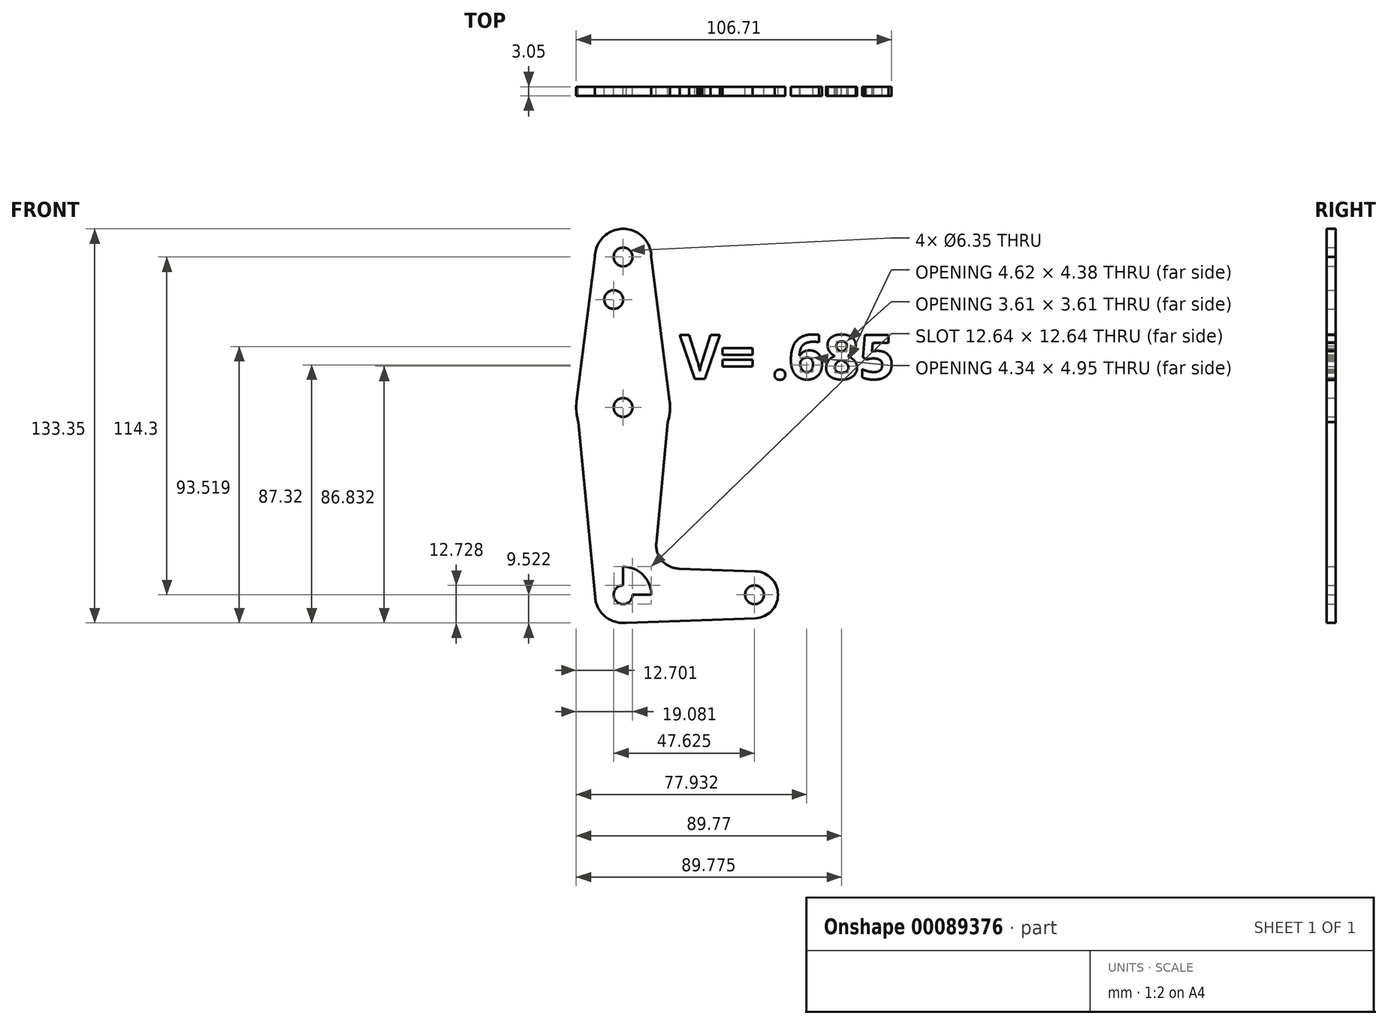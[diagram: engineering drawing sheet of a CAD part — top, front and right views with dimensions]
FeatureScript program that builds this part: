
annotation { "Feature Type Name" : "Feature", "Feature Type Description" : "" }
export const myFeature = defineFeature(function(context is Context, id is Id, definition is map)
    precondition{}
    {
        {
            var Q0;
            Q0=qCreatedBy(makeId("Front.planeOp"),FACE);
            var sketch = newSketch(context, id + "F0", { "sketchPlane" : qUnion([Q0])});
            skCircle(sketch, "E0", {"center": v(-39.47, 60.23) * mm, "radius": 9.53 * mm});
            skCircle(sketch, "E1", {"center": v(-39.47, 9.3) * mm, "radius": 15.88 * mm});
            skLineSegment(sketch, "E2", {"start": v(-39.47, 60.23) * mm, "end": v(-39.47, -54.07) * mm});
            skLineSegment(sketch, "E3", {"start": v(-39.47, -54.07) * mm, "end": v(4.98, -54.07) * mm});
            skCircle(sketch, "E4", {"center": v(-39.47, -54.07) * mm, "radius": 9.53 * mm});
            skCircle(sketch, "E5", {"center": v(4.98, -54.07) * mm, "radius": 7.94 * mm});
            skLineSegment(sketch, "E6", {"start": v(-49, 60.23) * mm, "end": v(-55.22, 11.3) * mm});
            skLineSegment(sketch, "E7", {"start": v(-55.22, 11.3) * mm, "end": v(-48.96, -54.96) * mm});
            skLineSegment(sketch, "E8", {"start": v(-29.95, 60.21) * mm, "end": v(-23.73, 11.3) * mm});
            skLineSegment(sketch, "E9", {"start": v(-23.73, 11.3) * mm, "end": v(-28.25, -36.52) * mm});
            skLineSegment(sketch, "E10", {"start": v(-20.62, -45.21) * mm, "end": v(5.26, -46.14) * mm});
            skCircle(sketch, "E11", {"center": v(-39.47, 60.23) * mm, "radius": 3.18 * mm});
            skCircle(sketch, "E12", {"center": v(-39.47, 9.3) * mm, "radius": 3.18 * mm});
            skCircle(sketch, "E13", {"center": v(-39.47, -54.07) * mm, "radius": 3.18 * mm});
            skCircle(sketch, "E14", {"center": v(4.98, -54.07) * mm, "radius": 3.18 * mm});
            skLineSegment(sketch, "E15", {"start": v(-39.47, 45.83) * mm, "end": v(-42.65, 45.83) * mm});
            skCircle(sketch, "E16", {"center": v(-42.65, 45.83) * mm, "radius": 3.18 * mm});
            skArc(sketch, "E17.filletArc", {"start": v(-28.25, -36.52) * mm, "mid": v(-26.3, -42.51) * mm, "end": v(-20.62, -45.21) * mm});
            skLineSegment(sketch, "E18", {"start": v(-39.94, -63.58) * mm, "end": v(5.25, -62) * mm});
            skText(sketch, "E19", { "text": "V= .685", "fontName": "OpenSans-Bold.ttf"});
            const initialGuessF0  = {"E19": [-0.02031, 0.01894, 1, 0, 0.01503]};
            skSetInitialGuess(sketch, initialGuessF0);
            skSolve(sketch);
        }
        {
            var Q0;
            Q0 = qSketchRegion(id + "F0", true);
            extrude(context, id + "F1", {"entities" : qUnion([Q0]), "depth" : 3.05 * mm});
        }
    });
